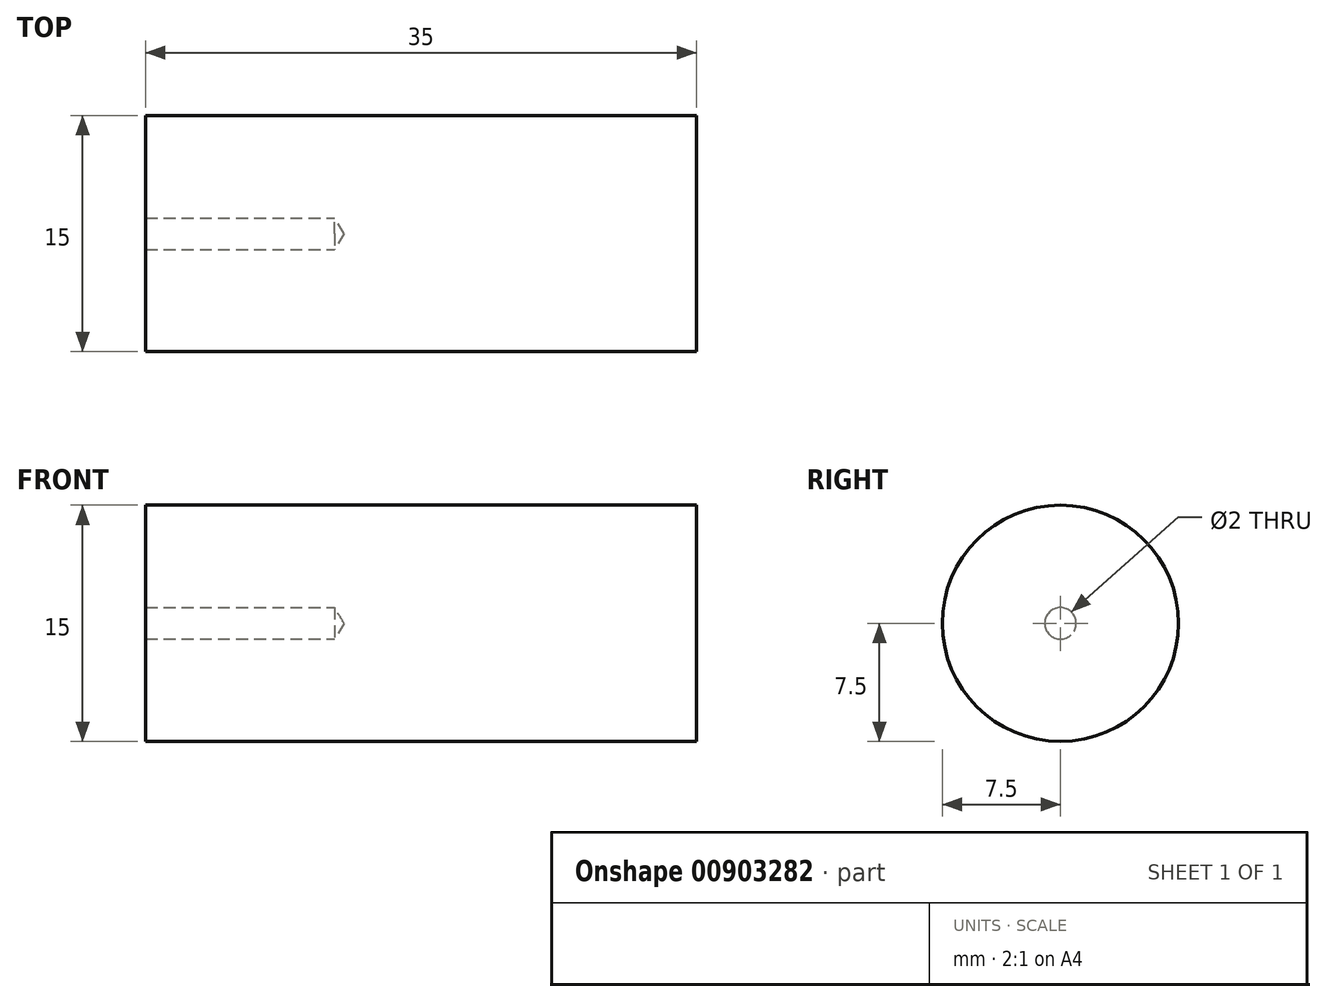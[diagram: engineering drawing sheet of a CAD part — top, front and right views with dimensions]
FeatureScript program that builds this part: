
annotation { "Feature Type Name" : "Feature", "Feature Type Description" : "" }
export const myFeature = defineFeature(function(context is Context, id is Id, definition is map)
    precondition{}
    {
        {
            var Q0;
            Q0=qCreatedBy(makeId("Right.planeOp"),FACE);
            var sketch = newSketch(context, id + "F0", { "sketchPlane" : qUnion([Q0])});
            skCircle(sketch, "E0", {"center": v(0, 45) * mm, "radius": 7.5 * mm});
            skLineSegment(sketch, "E1", {"start": v(0, 0) * mm, "end": v(0, 45) * mm, "construction": true});
            skSolve(sketch);
        }
        {
            var Q0;
            Q0 = qSketchRegion(id + "F0", true);
            extrude(context, id + "F1", {"entities" : qUnion([Q0]), "depth" : 35 * mm, "offsetDistance" : 25 * mm});
        }
        {
            var Q0;
            Q0=makeQuery(id+"F1.opExtrude","CAP_FACE",FACE,{"disambiguationData":[OSD([sQuery(id+"F0.wireOp",EDGE,"E0")])],"isStart":true});
            var sketch = newSketch(context, id + "F2", { "sketchPlane" : qUnion([Q0])});
            skPoint(sketch, "E2", {"position": v(0, 45) * mm});
            skSolve(sketch);
        }
        {
            var Q0;
            Q0=sQuery(id+"F2.wireOp",VERTEX,"E2");
            var Q1;
            Q1=makeQuery(id+"F1.opExtrude","SWEPT_BODY",BODY,{"disambiguationData":[OSD([sQuery(id+"F0.wireOp",EDGE,"E0")])]});
            hole(context, id + "F3", {"style" : HoleStyle.SIMPLE, "endStyle" : HoleEndStyle.BLIND, "holeDiameter" : 2 * mm, "majorDiameter" : 5 * mm, "holeDepth" : 12 * mm, "isTappedThrough" : true, "tappedDepth" : 12 * mm, "tapClearance" : 3, "locations" : qUnion([Q0]), "scope" : qUnion([Q1])});
        }
    });
